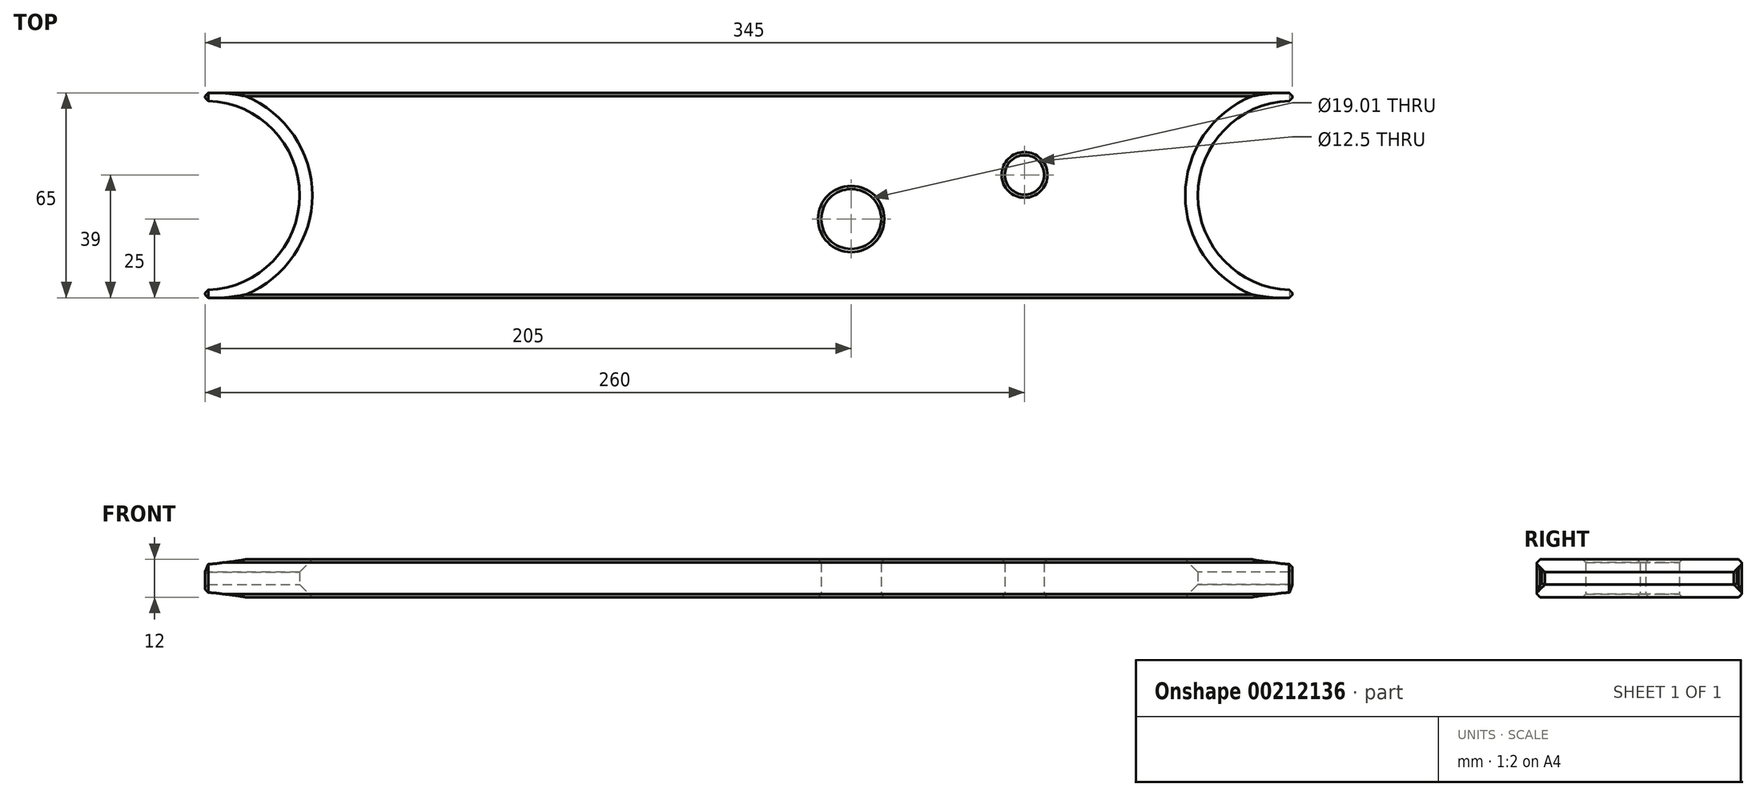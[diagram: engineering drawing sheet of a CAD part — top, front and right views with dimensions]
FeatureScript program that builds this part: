
annotation { "Feature Type Name" : "Feature", "Feature Type Description" : "" }
export const myFeature = defineFeature(function(context is Context, id is Id, definition is map)
    precondition{}
    {
        {
            var Q0;
            Q0=qCreatedBy(makeId("Top.planeOp"),FACE);
            var sketch = newSketch(context, id + "F0", { "sketchPlane" : qUnion([Q0])});
            skLineSegment(sketch, "E0.bottom", {"start": v(-172.5, -32.5) * mm, "end": v(172.5, -32.5) * mm});
            skLineSegment(sketch, "E0.top", {"start": v(-172.5, 32.5) * mm, "end": v(172.5, 32.5) * mm});
            skLineSegment(sketch, "E0.left", {"start": v(-172.5, -32.5) * mm, "end": v(-172.5, 32.5) * mm});
            skLineSegment(sketch, "E0.right", {"start": v(172.5, -32.5) * mm, "end": v(172.5, 32.5) * mm});
            skPoint(sketch, "E0.middle", {"position": v(0, 0) * mm});
            skCircle(sketch, "E1", {"center": v(32.5, -7.5) * mm, "radius": 9.5 * mm});
            skLineSegment(sketch, "E2", {"start": v(-172.5, 30) * mm, "end": v(172.5, 30) * mm, "construction": true});
            skLineSegment(sketch, "E3", {"start": v(-172.5, -30) * mm, "end": v(172.5, -30) * mm, "construction": true});
            skLineSegment(sketch, "E4", {"start": v(142.5, -32.5) * mm, "end": v(142.5, 32.5) * mm, "construction": true});
            skLineSegment(sketch, "E5", {"start": v(172.5, 0) * mm, "end": v(-172.5, 0) * mm});
            skArc(sketch, "E6", {"start": v(172.5, 30) * mm, "mid": v(142.5, 0) * mm, "end": v(172.5, -30) * mm});
            skLineSegment(sketch, "E7", {"start": v(-142.5, -32.5) * mm, "end": v(-142.5, 32.5) * mm, "construction": true});
            skArc(sketch, "E8", {"start": v(-172.5, -30) * mm, "mid": v(-142.5, 0) * mm, "end": v(-172.5, 30) * mm});
            skCircle(sketch, "E9", {"center": v(87.5, 6.5) * mm, "radius": 6.25 * mm});
            skSolve(sketch);
        }
        {
            var Q0;
            {var subQ5=sQuery(id+"F0.wireOp",EDGE,"E0.top");Q0=makeQuery(id+"F0.imprint","IMPRINT",FACE,{"disambiguationData":[TD([[makeQuery(id+"F0.imprint","IMPRINT",EDGE,{"derivedFrom":subQ5}),-1.0]])]});}
            var Q1;
            {var subQ5=sQuery(id+"F0.wireOp",EDGE,"E0.bottom");Q1=makeQuery(id+"F0.imprint","IMPRINT",FACE,{"disambiguationData":[TD([[makeQuery(id+"F0.imprint","IMPRINT",EDGE,{"derivedFrom":subQ5}),1.0]])]});}
            extrude(context, id + "F1", {"entities" : qUnion([Q0, Q1]), "depth" : 12 * mm});
        }
        {
            var Q0;
            Q0=makeQuery(id+"F1.opExtrude","CAP_EDGE",EDGE,{"disambiguationData":[OSD([sQuery(id+"F0.wireOp",EDGE,"E6")])],"isStart":true});
            var Q1;
            Q1=makeQuery(id+"F1.opExtrude","CAP_EDGE",EDGE,{"disambiguationData":[OSD([sQuery(id+"F0.wireOp",EDGE,"E8")])],"isStart":false});
            var Q2;
            Q2=makeQuery(id+"F1.opExtrude","CAP_EDGE",EDGE,{"disambiguationData":[OSD([sQuery(id+"F0.wireOp",EDGE,"E6")])],"isStart":false});
            var Q3;
            Q3=makeQuery(id+"F1.opExtrude","CAP_EDGE",EDGE,{"disambiguationData":[OSD([sQuery(id+"F0.wireOp",EDGE,"E8")])],"isStart":true});
            chamfer(context, id + "F2", {"entities" : qUnion([Q0, Q1, Q2, Q3]), "width" : 4 * mm, "tangentPropagation" : true});
        }
        {
            var Q0;
            Q0=makeQuery(id+"F1.opExtrude","CAP_EDGE",EDGE,{"disambiguationData":[OSD([sQuery(id+"F0.wireOp",EDGE,"E0.top")])],"isStart":true});
            var Q1;
            Q1=makeQuery(id+"F1.opExtrude","CAP_EDGE",EDGE,{"disambiguationData":[OSD([sQuery(id+"F0.wireOp",EDGE,"E0.bottom")])],"isStart":true});
            var Q2;
            Q2=makeQuery(id+"F1.opExtrude","SWEPT_EDGE",EDGE,{"disambiguationData":[OSD([sQuery(id+"F0.wireOp",EDGE,"E0.bottom"),sQuery(id+"F0.wireOp",EDGE,"E0.right")])]});
            var Q3;
            {var subQ0=sQuery(id+"F0.wireOp",EDGE,"E6");var subQ1=sQuery(id+"F0.wireOp",EDGE,"E0.right");Q3=makeQuery(id+"F1.opExtrude","SWEPT_EDGE",EDGE,{"disambiguationData":[OSD([subQ1,subQ0]),TDD([makeQuery(id+"F0.imprint","INTERSECT",VERTEX,{"disambiguationData":[OD(1.0)],"derivedFrom":[subQ1,subQ0]})])]});}
            var Q4;
            {var subQ0=sQuery(id+"F0.wireOp",EDGE,"E0.right");var subQ1=sQuery(id+"F0.wireOp",EDGE,"E6");Q4=makeQuery(id+"F2.opChamfer","BLEND_EDGE",EDGE,{"blendedFrom":[makeQuery(id+"F1.opExtrude","CAP_EDGE",EDGE,{"disambiguationData":[OSD([subQ1])],"isStart":true}),makeQuery(id+"F1.opExtrude","SWEPT_FACE",FACE,{"disambiguationData":[OSD([subQ0]),TDD([makeQuery(id+"F0.imprint","IMPRINT",EDGE,{"disambiguationData":[TD([[makeQuery(id+"F0.imprint","INTERSECT",VERTEX,{"derivedFrom":[sQuery(id+"F0.wireOp",EDGE,"E0.bottom"),subQ0]}),-1.0]])],"derivedFrom":subQ0})])]})],"blendedInto":[makeQuery(id+"F1.opExtrude","SWEPT_FACE",FACE,{"disambiguationData":[OSD([subQ0]),TDD([makeQuery(id+"F0.imprint","IMPRINT",EDGE,{"disambiguationData":[TD([[makeQuery(id+"F0.imprint","INTERSECT",VERTEX,{"derivedFrom":[sQuery(id+"F0.wireOp",EDGE,"E0.bottom"),subQ0]}),-1.0]])],"derivedFrom":subQ0})])]})]});}
            var Q5;
            Q5=makeQuery(id+"F1.opExtrude","CAP_EDGE",EDGE,{"disambiguationData":[OSD([sQuery(id+"F0.wireOp",EDGE,"E0.bottom")])],"isStart":false});
            var Q6;
            Q6=makeQuery(id+"F1.opExtrude","CAP_EDGE",EDGE,{"disambiguationData":[OSD([sQuery(id+"F0.wireOp",EDGE,"E0.top")])],"isStart":false});
            var Q7;
            {var subQ0=sQuery(id+"F0.wireOp",EDGE,"E0.right");Q7=makeQuery(id+"F1.opExtrude","CAP_EDGE",EDGE,{"disambiguationData":[OSD([subQ0]),TDD([makeQuery(id+"F0.imprint","IMPRINT",EDGE,{"disambiguationData":[TD([[makeQuery(id+"F0.imprint","INTERSECT",VERTEX,{"derivedFrom":[sQuery(id+"F0.wireOp",EDGE,"E0.bottom"),subQ0]}),-1.0]])],"derivedFrom":subQ0})])],"isStart":false});}
            var Q8;
            {var subQ0=sQuery(id+"F0.wireOp",EDGE,"E0.right");Q8=makeQuery(id+"F1.opExtrude","CAP_EDGE",EDGE,{"disambiguationData":[OSD([subQ0]),TDD([makeQuery(id+"F0.imprint","IMPRINT",EDGE,{"disambiguationData":[TD([[makeQuery(id+"F0.imprint","INTERSECT",VERTEX,{"derivedFrom":[sQuery(id+"F0.wireOp",EDGE,"E0.top"),subQ0]}),1.0]])],"derivedFrom":subQ0})])],"isStart":false});}
            var Q9;
            Q9=makeQuery(id+"F1.opExtrude","SWEPT_EDGE",EDGE,{"disambiguationData":[OSD([sQuery(id+"F0.wireOp",EDGE,"E0.top"),sQuery(id+"F0.wireOp",EDGE,"E0.right")])]});
            var Q10;
            {var subQ0=sQuery(id+"F0.wireOp",EDGE,"E6");var subQ1=sQuery(id+"F0.wireOp",EDGE,"E0.right");Q10=makeQuery(id+"F1.opExtrude","SWEPT_EDGE",EDGE,{"disambiguationData":[OSD([subQ1,subQ0]),TDD([makeQuery(id+"F0.imprint","INTERSECT",VERTEX,{"disambiguationData":[OD(0.0)],"derivedFrom":[subQ1,subQ0]})])]});}
            var Q11;
            {var subQ0=sQuery(id+"F0.wireOp",EDGE,"E0.right");var subQ1=sQuery(id+"F0.wireOp",EDGE,"E6");Q11=makeQuery(id+"F2.opChamfer","BLEND_EDGE",EDGE,{"blendedFrom":[makeQuery(id+"F1.opExtrude","CAP_EDGE",EDGE,{"disambiguationData":[OSD([subQ1])],"isStart":true}),makeQuery(id+"F1.opExtrude","SWEPT_FACE",FACE,{"disambiguationData":[OSD([subQ0]),TDD([makeQuery(id+"F0.imprint","IMPRINT",EDGE,{"disambiguationData":[TD([[makeQuery(id+"F0.imprint","INTERSECT",VERTEX,{"derivedFrom":[sQuery(id+"F0.wireOp",EDGE,"E0.top"),subQ0]}),1.0]])],"derivedFrom":subQ0})])]})],"blendedInto":[makeQuery(id+"F1.opExtrude","SWEPT_FACE",FACE,{"disambiguationData":[OSD([subQ0]),TDD([makeQuery(id+"F0.imprint","IMPRINT",EDGE,{"disambiguationData":[TD([[makeQuery(id+"F0.imprint","INTERSECT",VERTEX,{"derivedFrom":[sQuery(id+"F0.wireOp",EDGE,"E0.top"),subQ0]}),1.0]])],"derivedFrom":subQ0})])]})]});}
            var Q12;
            Q12=makeQuery(id+"F1.opExtrude","CAP_EDGE",EDGE,{"disambiguationData":[OSD([sQuery(id+"F0.wireOp",EDGE,"E1")])],"isStart":false});
            var Q13;
            Q13=makeQuery(id+"F1.opExtrude","CAP_EDGE",EDGE,{"disambiguationData":[OSD([sQuery(id+"F0.wireOp",EDGE,"E1")])],"isStart":true});
            var Q14;
            Q14=makeQuery(id+"F1.opExtrude","SWEPT_EDGE",EDGE,{"disambiguationData":[OSD([sQuery(id+"F0.wireOp",EDGE,"E0.bottom"),sQuery(id+"F0.wireOp",EDGE,"E0.left")])]});
            var Q15;
            {var subQ0=sQuery(id+"F0.wireOp",EDGE,"E8");var subQ1=sQuery(id+"F0.wireOp",EDGE,"E0.left");Q15=makeQuery(id+"F1.opExtrude","SWEPT_EDGE",EDGE,{"disambiguationData":[OSD([subQ1,subQ0]),TDD([makeQuery(id+"F0.imprint","INTERSECT",VERTEX,{"disambiguationData":[OD(1.0)],"derivedFrom":[subQ1,subQ0]})])]});}
            var Q16;
            Q16=makeQuery(id+"F1.opExtrude","SWEPT_EDGE",EDGE,{"disambiguationData":[OSD([sQuery(id+"F0.wireOp",EDGE,"E0.top"),sQuery(id+"F0.wireOp",EDGE,"E0.left")])]});
            var Q17;
            {var subQ0=sQuery(id+"F0.wireOp",EDGE,"E0.left");var subQ1=sQuery(id+"F0.wireOp",EDGE,"E8");Q17=makeQuery(id+"F2.opChamfer","BLEND_EDGE",EDGE,{"blendedFrom":[makeQuery(id+"F1.opExtrude","CAP_EDGE",EDGE,{"disambiguationData":[OSD([subQ1])],"isStart":false}),makeQuery(id+"F1.opExtrude","SWEPT_FACE",FACE,{"disambiguationData":[OSD([subQ0]),TDD([makeQuery(id+"F0.imprint","IMPRINT",EDGE,{"disambiguationData":[TD([[makeQuery(id+"F0.imprint","INTERSECT",VERTEX,{"derivedFrom":[sQuery(id+"F0.wireOp",EDGE,"E0.top"),subQ0]}),1.0]])],"derivedFrom":subQ0})])]})],"blendedInto":[makeQuery(id+"F1.opExtrude","SWEPT_FACE",FACE,{"disambiguationData":[OSD([subQ0]),TDD([makeQuery(id+"F0.imprint","IMPRINT",EDGE,{"disambiguationData":[TD([[makeQuery(id+"F0.imprint","INTERSECT",VERTEX,{"derivedFrom":[sQuery(id+"F0.wireOp",EDGE,"E0.top"),subQ0]}),1.0]])],"derivedFrom":subQ0})])]})]});}
            var Q18;
            {var subQ0=sQuery(id+"F0.wireOp",EDGE,"E0.left");Q18=makeQuery(id+"F1.opExtrude","CAP_EDGE",EDGE,{"disambiguationData":[OSD([subQ0]),TDD([makeQuery(id+"F0.imprint","IMPRINT",EDGE,{"disambiguationData":[TD([[makeQuery(id+"F0.imprint","INTERSECT",VERTEX,{"derivedFrom":[sQuery(id+"F0.wireOp",EDGE,"E0.top"),subQ0]}),1.0]])],"derivedFrom":subQ0})])],"isStart":true});}
            var Q19;
            {var subQ0=sQuery(id+"F0.wireOp",EDGE,"E0.left");Q19=makeQuery(id+"F1.opExtrude","CAP_EDGE",EDGE,{"disambiguationData":[OSD([subQ0]),TDD([makeQuery(id+"F0.imprint","IMPRINT",EDGE,{"disambiguationData":[TD([[makeQuery(id+"F0.imprint","INTERSECT",VERTEX,{"derivedFrom":[sQuery(id+"F0.wireOp",EDGE,"E0.bottom"),subQ0]}),-1.0]])],"derivedFrom":subQ0})])],"isStart":true});}
            var Q20;
            {var subQ0=sQuery(id+"F0.wireOp",EDGE,"E8");var subQ1=sQuery(id+"F0.wireOp",EDGE,"E0.left");Q20=makeQuery(id+"F1.opExtrude","SWEPT_EDGE",EDGE,{"disambiguationData":[OSD([subQ1,subQ0]),TDD([makeQuery(id+"F0.imprint","INTERSECT",VERTEX,{"disambiguationData":[OD(0.0)],"derivedFrom":[subQ1,subQ0]})])]});}
            var Q21;
            {var subQ0=sQuery(id+"F0.wireOp",EDGE,"E0.left");var subQ1=sQuery(id+"F0.wireOp",EDGE,"E8");Q21=makeQuery(id+"F2.opChamfer","BLEND_EDGE",EDGE,{"blendedFrom":[makeQuery(id+"F1.opExtrude","CAP_EDGE",EDGE,{"disambiguationData":[OSD([subQ1])],"isStart":false}),makeQuery(id+"F1.opExtrude","SWEPT_FACE",FACE,{"disambiguationData":[OSD([subQ0]),TDD([makeQuery(id+"F0.imprint","IMPRINT",EDGE,{"disambiguationData":[TD([[makeQuery(id+"F0.imprint","INTERSECT",VERTEX,{"derivedFrom":[sQuery(id+"F0.wireOp",EDGE,"E0.bottom"),subQ0]}),-1.0]])],"derivedFrom":subQ0})])]})],"blendedInto":[makeQuery(id+"F1.opExtrude","SWEPT_FACE",FACE,{"disambiguationData":[OSD([subQ0]),TDD([makeQuery(id+"F0.imprint","IMPRINT",EDGE,{"disambiguationData":[TD([[makeQuery(id+"F0.imprint","INTERSECT",VERTEX,{"derivedFrom":[sQuery(id+"F0.wireOp",EDGE,"E0.bottom"),subQ0]}),-1.0]])],"derivedFrom":subQ0})])]})]});}
            var Q22;
            Q22=makeQuery(id+"F1.opExtrude","CAP_EDGE",EDGE,{"disambiguationData":[OSD([sQuery(id+"F0.wireOp",EDGE,"E9")])],"isStart":false});
            var Q23;
            Q23=makeQuery(id+"F1.opExtrude","CAP_EDGE",EDGE,{"disambiguationData":[OSD([sQuery(id+"F0.wireOp",EDGE,"E9")])],"isStart":true});
            chamfer(context, id + "F3", {"entities" : qUnion([Q0, Q1, Q2, Q3, Q4, Q5, Q6, Q7, Q8, Q9, Q10, Q11, Q12, Q13, Q14, Q15, Q16, Q17, Q18, Q19, Q20, Q21, Q22, Q23]), "width" : 1 * mm, "tangentPropagation" : true});
        }
    });
